# Revit family: Eurolan_Шкафы Rackcenter D9000
name_source: partatom
category: Электрооборудование
units: mm (PartAtom-declared; Revit-internal decimal feet)

## family parameters
Всегда вертикально = Да
На основе рабочей плоскости = Нет
Общий = Нет
При загрузке вырезать с полостями = Нет
Размер круглого соединителя = Использовать диаметр
Тип детали = Другая панель
Точка расчета площади = Нет

## types (32) — shared parameters
ADSK_Единица измерения = шт.
ADSK_Завод-изготовитель = Eurolan
ADSK_Марка = D9000
ADSK_Материал = Металл RAL 9005
ADSK_Наименование краткое = 19" шкаф Rackcenter D9000
Смещение от пола = 51 мм
выбор_задняя дверь = in_Дверь_перфорированная_двойная

## per-type parameters (varying)
| type | 48U | ADSK_Код изделия | ADSK_Масса | ADSK_Наименование | ADSK_Размер_Высота | ADSK_Размер_Глубина | ADSK_Размер_Ширина | Боковые панели | Глубина зоны обслуживания_Сзади | Глубина зоны обслуживания_Спереди | выбор_передняя дверь | число_передняя дверь |
| 42U_600×1000_60F-42-6A-94BL_19" шкаф Rackcenter D9000_передняя дверь одностворчатая, задняя дверь двустворчатая | Нет | 60F-42-6A-94BL | 140 | 19" шкаф Rackcenter D9000, 42U 600 × 1000 мм, передняя дверь перфорированная одностворчатая, задняя дверь перфорированная двустворчатая, черный | 2044 мм | 1000 мм | 600 мм | Да | 300 мм | 600 мм | in_Дверь_перфорированная_одинарная | 1 |
| 42U_600×1000_60F-42-6A-95BL_19" шкаф Rackcenter D9000_передняя дверь двустворчатая, задняя дверь двустворчатая | Нет | 60F-42-6A-95BL | 140 | 19" шкаф Rackcenter D9000, 42U 600 × 1000 мм, передняя дверь перфорированная двустворчатая, задняя дверь перфорированная двустворчатая,черный | 2044 мм | 1000 мм | 600 мм | Да | 300 мм | 300 мм | in_Дверь_перфорированная_двойная | 2 |
| 42U_600×1000_60F-42-6A-96BL_19" шкаф Rackcenter D9000_передняя дверь одностворчатая, задняя дверь двустворчатая_без боковых стенок | Нет | 60F-42-6A-96BL | 112.2 | 19" шкаф Rackcenter D9000, 42U 600 × 1000 мм, передняя дверь перфорированная одностворчатая, задняя дверь перфорированная двустворчатая, без боковых стенок, черный | 2044 мм | 1000 мм | 600 мм | Нет | 300 мм | 600 мм | in_Дверь_перфорированная_одинарная | 1 |
| 42U_600×1000_60F-42-6A-97BL_19" шкаф Rackcenter D9000_передняя дверь двустворчатая, задняя дверь двустворчатая_без боковых стенок | Нет | 60F-42-6A-97BL | 112.2 | 19" шкаф Rackcenter D9000, 42U 600 × 1000 мм, передняя дверь перфорированная двустворчатая, задняя дверь перфорированная двустворчатая, без боковых стенок, черный | 2044 мм | 1000 мм | 600 мм | Нет | 300 мм | 300 мм | in_Дверь_перфорированная_двойная | 2 |
| 42U_600×1200_60F-42-6C-94BL_19" шкаф Rackcenter D9000_передняя дверь одностворчатая, задняя дверь двустворчатая | Нет | 60F-42-6C-94BL | 160 | 19" шкаф Rackcenter D9000, 42U 600 × 1200 мм, передняя дверь перфорированная одностворчатая, задняя дверь перфорированная двустворчатая, черный | 2044 мм | 1200 мм | 600 мм | Да | 300 мм | 600 мм | in_Дверь_перфорированная_одинарная | 1 |
| 42U_600×1200_60F-42-6C-95BL_19" шкаф Rackcenter D9000_передняя дверь двустворчатая, задняя дверь двустворчатая | Нет | 60F-42-6C-95BL | 160 | 19" шкаф Rackcenter D9000, 42U 600 × 1200 мм, передняя дверь перфорированная двустворчатая, задняя дверь перфорированная двустворчатая,черный | 2044 мм | 1200 мм | 600 мм | Да | 300 мм | 300 мм | in_Дверь_перфорированная_двойная | 2 |
| 42U_600×1200_60F-42-6C-96BL_19" шкаф Rackcenter D9000_передняя дверь одностворчатая, задняя дверь двустворчатая_без боковых стенок | Нет | 60F-42-6C-96BL | 127.4 | 19" шкаф Rackcenter D9000, 42U 600 × 1200 мм, передняя дверь перфорированная одностворчатая, задняя дверь перфорированная двустворчатая, без боковых стенок, черный | 2044 мм | 1200 мм | 600 мм | Нет | 300 мм | 600 мм | in_Дверь_перфорированная_одинарная | 1 |
| 42U_600×1200_60F-42-6C-97BL_19" шкаф Rackcenter D9000_передняя дверь двустворчатая, задняя дверь двустворчатая_без боковых стенок | Нет | 60F-42-6C-97BL | 127.4 | 19" шкаф Rackcenter D9000, 42U 600 × 1200 мм, передняя дверь перфорированная двустворчатая, задняя дверь перфорированная двустворчатая, без боковых стенок, черный | 2044 мм | 1200 мм | 600 мм | Нет | 300 мм | 300 мм | in_Дверь_перфорированная_двойная | 2 |
| 42U_750×1000_60F-42-7A-94BL_19" шкаф Rackcenter D9000_передняя дверь одностворчатая, задняя дверь двустворчатая | Нет | 60F-42-7A-94BL | 180 | 19" шкаф Rackcenter D9000, 42U 750 × 1000 мм, передняя дверь перфорированная одностворчатая, задняя дверь перфорированная двустворчатая, черный | 2044 мм | 1000 мм | 750 мм | Да | 375 мм | 750 мм | in_Дверь_перфорированная_одинарная | 1 |
| 42U_750×1000_60F-42-7A-95BL_19" шкаф Rackcenter D9000_передняя дверь двустворчатая, задняя дверь двустворчатая | Нет | 60F-42-7A-95BL | 180 | 19" шкаф Rackcenter D9000, 42U 750 × 1000 мм, передняя дверь перфорированная двустворчатая, задняя дверь перфорированная двустворчатая,черный | 2044 мм | 1000 мм | 750 мм | Да | 375 мм | 375 мм | in_Дверь_перфорированная_двойная | 2 |
| 42U_750×1000_60F-42-7A-96BL_19" шкаф Rackcenter D9000_передняя дверь одностворчатая, задняя дверь двустворчатая_без боковых стенок | Нет | 60F-42-7A-96BL | 152.2 | 19" шкаф Rackcenter D9000, 42U 750 × 1000 мм, передняя дверь перфорированная одностворчатая, задняя дверь перфорированная двустворчатая, без боковых стенок, черный | 2044 мм | 1000 мм | 750 мм | Нет | 375 мм | 750 мм | in_Дверь_перфорированная_одинарная | 1 |
| 42U_750×1000_60F-42-7A-97BL_19" шкаф Rackcenter D9000_передняя дверь двустворчатая, задняя дверь двустворчатая_без боковых стенок | Нет | 60F-42-7A-97BL | 152.2 | 19" шкаф Rackcenter D9000, 42U 750 × 1000 мм, передняя дверь перфорированная двустворчатая, задняя дверь перфорированная двустворчатая, без боковых стенок, черный | 2044 мм | 1000 мм | 750 мм | Нет | 375 мм | 375 мм | in_Дверь_перфорированная_двойная | 2 |
| 42U_750×1200_60F-42-7C-94BL_19" шкаф Rackcenter D9000_передняя дверь одностворчатая, задняя дверь двустворчатая | Нет | 60F-42-7C-94BL | 185 | 19" шкаф Rackcenter D9000, 42U 750 × 1200 мм, передняя дверь перфорированная одностворчатая, задняя дверь перфорированная двустворчатая, черный | 2044 мм | 1200 мм | 750 мм | Да | 375 мм | 750 мм | in_Дверь_перфорированная_одинарная | 1 |
| 42U_750×1200_60F-42-7C-95BL_19" шкаф Rackcenter D9000_передняя дверь двустворчатая, задняя дверь двустворчатая | Нет | 60F-42-7C-95BL | 185 | 19" шкаф Rackcenter D9000, 42U 750 × 1200 мм, передняя дверь перфорированная двустворчатая, задняя дверь перфорированная двустворчатая,черный | 2044 мм | 1200 мм | 750 мм | Да | 375 мм | 375 мм | in_Дверь_перфорированная_двойная | 2 |
| 42U_750×1200_60F-42-7C-96BL_19" шкаф Rackcenter D9000_передняя дверь одностворчатая, задняя дверь двустворчатая_без боковых стенок | Нет | 60F-42-7C-96BL | 142.4 | 19" шкаф Rackcenter D9000, 42U 750 × 1200 мм, передняя дверь перфорированная одностворчатая, задняя дверь перфорированная двустворчатая, без боковых стенок, черный | 2044 мм | 1200 мм | 750 мм | Нет | 375 мм | 750 мм | in_Дверь_перфорированная_одинарная | 1 |
| 42U_750×1200_60F-42-7C-97BL_19" шкаф Rackcenter D9000_передняя дверь двустворчатая, задняя дверь двустворчатая_без боковых стенок | Нет | 60F-42-7C-97BL | 142.4 | 19" шкаф Rackcenter D9000, 42U 750 × 1200 мм, передняя дверь перфорированная двустворчатая, задняя дверь перфорированная двустворчатая, без боковых стенок, черный | 2044 мм | 1200 мм | 750 мм | Нет | 375 мм | 375 мм | in_Дверь_перфорированная_двойная | 2 |
| 48U_750×1200_60F-48-7C-97BL_19" шкаф Rackcenter D9000_передняя дверь двустворчатая, задняя дверь двустворчатая_без боковых стенок | Да | 60F-48-7C-97BL | 173.8 | 19" шкаф Rackcenter D9000, 48U 750 × 1200 мм, передняя дверь перфорированная двустворчатая, задняя дверь перфорированная двустворчатая, без боковых стенок, черный | 2320 мм | 1200 мм | 750 мм | Нет | 375 мм | 375 мм | in_Дверь_перфорированная_двойная | 2 |
| 48U_600×1000_60F-48-6A-94BL_19" шкаф Rackcenter D9000_передняя дверь одностворчатая, задняя дверь двустворчатая | Да | 60F-48-6A-94BL | 165 | 19" шкаф Rackcenter D9000, 48U 600 × 1000 мм, передняя дверь перфорированная одностворчатая, задняя дверь перфорированная двустворчатая, черный | 2320 мм | 1000 мм | 600 мм | Да | 300 мм | 600 мм | in_Дверь_перфорированная_одинарная | 1 |
| 48U_600×1000_60F-48-6A-95BL_19" шкаф Rackcenter D9000_передняя дверь двустворчатая, задняя дверь двустворчатая | Да | 60F-48-6A-95BL | 165 | 19" шкаф Rackcenter D9000, 48U 600 × 1000 мм, передняя дверь перфорированная двустворчатая, задняя дверь перфорированная двустворчатая,черный | 2320 мм | 1000 мм | 600 мм | Да | 300 мм | 300 мм | in_Дверь_перфорированная_двойная | 2 |
| 48U_750×1000_60F-48-7A-97BL_19" шкаф Rackcenter D9000_передняя дверь двустворчатая, задняя дверь двустворчатая_без боковых стенок | Да | 60F-48-7A-97BL | 173.2 | 19" шкаф Rackcenter D9000, 48U 750 × 1000 мм, передняя дверь перфорированная двустворчатая, задняя дверь перфорированная двустворчатая, без боковых стенок, черный | 2320 мм | 1000 мм | 750 мм | Нет | 375 мм | 375 мм | in_Дверь_перфорированная_двойная | 2 |
| 48U_600×1000_60F-48-6A-97BL_19" шкаф Rackcenter D9000_передняя дверь двустворчатая, задняя дверь двустворчатая_без боковых стенок | Да | 60F-48-6A-97BL | 133.2 | 19" шкаф Rackcenter D9000, 48U 600 × 1000 мм, передняя дверь перфорированная двустворчатая, задняя дверь перфорированная двустворчатая, без боковых стенок, черный | 2320 мм | 1000 мм | 600 мм | Нет | 300 мм | 300 мм | in_Дверь_перфорированная_двойная | 2 |
| 48U_750×1000_60F-48-7A-94BL_19" шкаф Rackcenter D9000_передняя дверь одностворчатая, задняя дверь двустворчатая | Да | 60F-48-7A-94BL | 205 | 19" шкаф Rackcenter D9000, 48U 750 × 1000 мм, передняя дверь перфорированная одностворчатая, задняя дверь перфорированная двустворчатая, черный | 2320 мм | 1000 мм | 750 мм | Да | 375 мм | 750 мм | in_Дверь_перфорированная_одинарная | 0 |
| 48U_750×1200_60F-48-7C-95BL_19" шкаф Rackcenter D9000_передняя дверь двустворчатая, задняя дверь двустворчатая | Да | 60F-48-7C-95BL | 210 | 19" шкаф Rackcenter D9000, 48U 750 × 1200 мм, передняя дверь перфорированная двустворчатая, задняя дверь перфорированная двустворчатая,черный | 2320 мм | 1200 мм | 750 мм | Да | 375 мм | 375 мм | in_Дверь_перфорированная_двойная | 2 |
| 48U_600×1200_60F-48-6C-95BL_19" шкаф Rackcenter D9000_передняя дверь двустворчатая, задняя дверь двустворчатая | Да | 60F-48-6C-95BL | 185 | 19" шкаф Rackcenter D9000, 48U 600 × 1200 мм, передняя дверь перфорированная двустворчатая, задняя дверь перфорированная двустворчатая,черный | 2320 мм | 1200 мм | 600 мм | Да | 300 мм | 300 мм | in_Дверь_перфорированная_двойная | 2 |
| 48U_600×1000_60F-48-6A-96BL_19" шкаф Rackcenter D9000_передняя дверь одностворчатая, задняя дверь двустворчатая_без боковых стенок | Да | 60F-48-6A-96BL | 133.2 | 19" шкаф Rackcenter D9000, 48U 600 × 1000 мм, передняя дверь перфорированная одностворчатая, задняя дверь перфорированная двустворчатая, без боковых стенок, черный | 2320 мм | 1000 мм | 600 мм | Нет | 300 мм | 600 мм | in_Дверь_перфорированная_одинарная | 0 |
| 48U_600×1200_60F-48-6C-96BL_19" шкаф Rackcenter D9000_передняя дверь одностворчатая, задняя дверь двустворчатая_без боковых стенок | Да | 60F-48-6C-96BL | 148.8 | 19" шкаф Rackcenter D9000, 48U 600 × 1200 мм, передняя дверь перфорированная одностворчатая, задняя дверь перфорированная двустворчатая, без боковых стенок, черный | 2320 мм | 1200 мм | 600 мм | Нет | 300 мм | 600 мм | in_Дверь_перфорированная_одинарная | 0 |
| 48U_600×1200_60F-48-6C-94BL_19" шкаф Rackcenter D9000_передняя дверь одностворчатая, задняя дверь двустворчатая | Да | 60F-48-6C-94BL | 185 | 19" шкаф Rackcenter D9000, 48U 600 × 1200 мм, передняя дверь перфорированная одностворчатая, задняя дверь перфорированная двустворчатая, черный | 2320 мм | 1200 мм | 600 мм | Да | 300 мм | 600 мм | in_Дверь_перфорированная_одинарная | 0 |
| 48U_600×1200_60F-48-6C-97BL_19" шкаф Rackcenter D9000_передняя дверь двустворчатая, задняя дверь двустворчатая_без боковых стенок | Да | 60F-48-6C-97BL | 148.8 | 19" шкаф Rackcenter D9000, 48U 600 × 1200 мм, передняя дверь перфорированная двустворчатая, задняя дверь перфорированная двустворчатая, без боковых стенок, черный | 2320 мм | 1200 мм | 600 мм | Нет | 300 мм | 300 мм | in_Дверь_перфорированная_двойная | 2 |
| 48U_750×1000_60F-48-7A-96BL_19" шкаф Rackcenter D9000_передняя дверь одностворчатая, задняя дверь двустворчатая_без боковых стенок | Да | 60F-48-7A-96BL | 173.2 | 19" шкаф Rackcenter D9000, 48U 750 × 1000 мм, передняя дверь перфорированная одностворчатая, задняя дверь перфорированная двустворчатая, без боковых стенок, черный | 2320 мм | 1000 мм | 750 мм | Нет | 375 мм | 750 мм | in_Дверь_перфорированная_одинарная | 0 |
| 48U_750×1000_60F-48-7A-95BL_19" шкаф Rackcenter D9000_передняя дверь двустворчатая, задняя дверь двустворчатая | Да | 60F-48-7A-95BL | 205 | 19" шкаф Rackcenter D9000, 48U 750 × 1000 мм, передняя дверь перфорированная двустворчатая, задняя дверь перфорированная двустворчатая,черный | 2320 мм | 1000 мм | 750 мм | Да | 375 мм | 375 мм | in_Дверь_перфорированная_двойная | 2 |
| 48U_750×1200_60F-48-7C-96BL_19" шкаф Rackcenter D9000_передняя дверь одностворчатая, задняя дверь двустворчатая_без боковых стенок | Да | 60F-48-7C-96BL | 173.8 | 19" шкаф Rackcenter D9000, 48U 750 × 1200 мм, передняя дверь перфорированная одностворчатая, задняя дверь перфорированная двустворчатая, без боковых стенок, черный | 2320 мм | 1200 мм | 750 мм | Нет | 375 мм | 750 мм | in_Дверь_перфорированная_одинарная | 0 |
| 48U_750×1200_60F-48-7C-94BL_19" шкаф Rackcenter D9000_передняя дверь одностворчатая, задняя дверь двустворчатая | Да | 60F-48-7C-94BL | 210 | 19" шкаф Rackcenter D9000, 48U 750 × 1200 мм, передняя дверь перфорированная одностворчатая, задняя дверь перфорированная двустворчатая, черный | 2320 мм | 1200 мм | 750 мм | Да | 375 мм | 750 мм | in_Дверь_перфорированная_одинарная | 0 |
